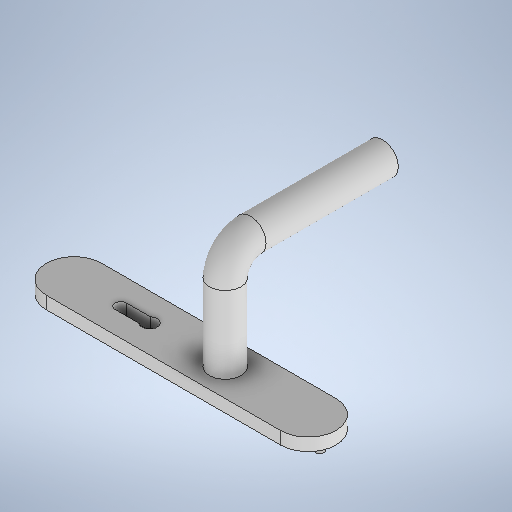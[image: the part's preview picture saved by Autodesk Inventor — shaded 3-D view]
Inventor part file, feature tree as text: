
AUTODESK INVENTOR PART (.ipt)
format: ipt  version: 2025.1 (Build 291241000, 241)  size: 304,128 bytes
history: native  units: mm
features: sketch x5, extrude x3, other x1, plane x1, sweep x1, projected_geometry x1
ambient origin geometry x8: Origin, YZ Plane, XZ Plane, XY Plane, X Axis, Y Axis, Z Axis, Center Point
bodies: Body1 (feature_tree)
feature tree (12):
  sketch  "Sketch1"  dims[d0=25.0mm d1=61.0mm]
  sketch  "Sketch2"  dims[d8=0.0mm d9=0.0mm d10=44.0mm]
  other  "Work Point1"
  plane  "Work Plane1"
  sweep  "Sweep2"
  extrude  "Extrusion1"  Depth=44.0mm
  extrude  "Extrusion2"  Depth=230.0mm
  extrude  "Extrusion3"  Depth=10.0mm
  sketch  "Sketch4"  dims[d12=88.0mm d13=230.0mm]
  projected_geometry  "Projected Loop1"
  sketch  "Sketch5"  dims[d14=10.0mm d15=0.0mm d16=7.0mm]
  sketch  "Sketch6"  dims[d17=21.5mm d18=75.0mm d19=90.5mm d20=10.0mm d21=0.0mm d22=12.0mm d23=60.0mm d24=4.5mm d25=23.0mm d26=10.0mm d27=0.0mm d30=105.0mm d31=20.0mm]
